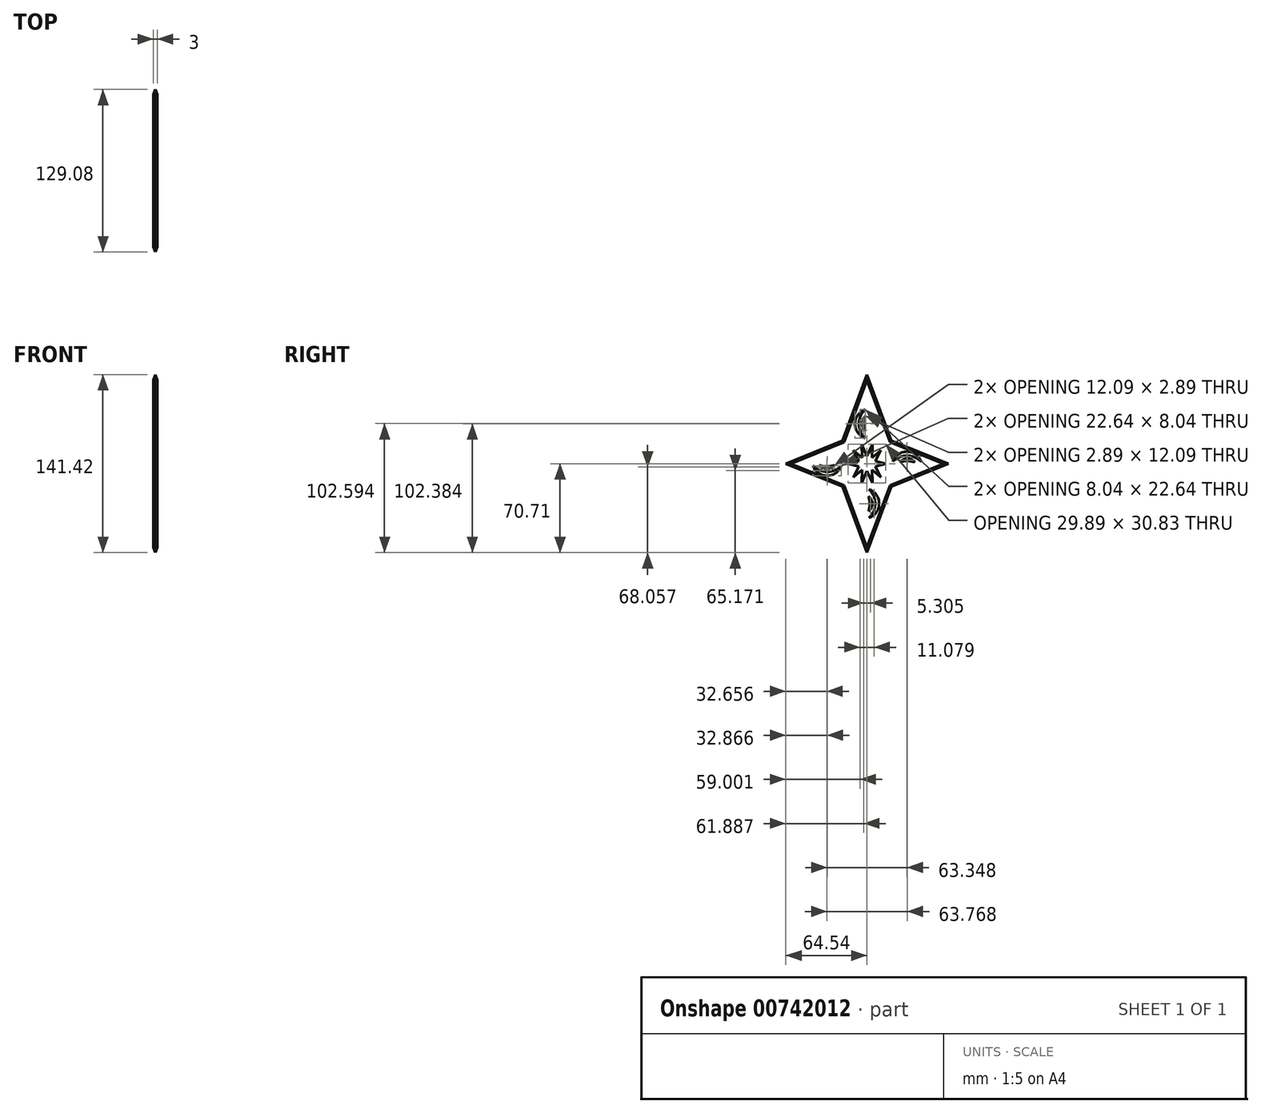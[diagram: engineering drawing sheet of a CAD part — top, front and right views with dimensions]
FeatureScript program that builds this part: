
annotation { "Feature Type Name" : "Feature", "Feature Type Description" : "" }
export const myFeature = defineFeature(function(context is Context, id is Id, definition is map)
    precondition{}
    {
        {
            var Q0;
            Q0=qCreatedBy(makeId("Right.planeOp"),FACE);
            var sketch = newSketch(context, id + "F0", { "sketchPlane" : qUnion([Q0])});
            skLineSegment(sketch, "E0", {"start": v(0, -70.7) * mm, "end": v(-19.36, -18.32) * mm});
            skLineSegment(sketch, "E1", {"start": v(-19.36, -18.32) * mm, "end": v(-64.54, 0) * mm});
            skLineSegment(sketch, "E2.MirrorCS", {"start": v(0, -70.7) * mm, "end": v(19.36, -18.32) * mm});
            skLineSegment(sketch, "E3.MirrorCS", {"start": v(19.36, -18.32) * mm, "end": v(64.54, 0) * mm});
            skLineSegment(sketch, "E4.MirrorCS", {"start": v(-19.36, 18.32) * mm, "end": v(-64.54, 0) * mm});
            skLineSegment(sketch, "E5.MirrorCS", {"start": v(0, 70.7) * mm, "end": v(-19.36, 18.32) * mm});
            skLineSegment(sketch, "E6.MirrorCS", {"start": v(0, 70.7) * mm, "end": v(19.36, 18.32) * mm});
            skLineSegment(sketch, "E7.MirrorCS", {"start": v(19.36, 18.32) * mm, "end": v(64.54, 0) * mm});
            skSolve(sketch);
        }
        {
            var Q0;
            Q0=qSketchRegion(id+"F0",true);
            extrude(context, id + "F1", {"entities" : qUnion([Q0]), "depth" : 3 * mm});
        }
        {
            var Q0;
            Q0=makeQuery(id+"F1.opExtrude","CAP_EDGE",EDGE,{"disambiguationData":[OSD([sQuery(id+"F0.wireOp",EDGE,"E4.MirrorCS")])],"isStart":false});
            var Q1;
            Q1=makeQuery(id+"F1.opExtrude","CAP_EDGE",EDGE,{"disambiguationData":[OSD([sQuery(id+"F0.wireOp",EDGE,"E5.MirrorCS")])],"isStart":false});
            var Q2;
            Q2=makeQuery(id+"F1.opExtrude","CAP_EDGE",EDGE,{"disambiguationData":[OSD([sQuery(id+"F0.wireOp",EDGE,"E5.MirrorCS")])],"isStart":true});
            var Q3;
            Q3=makeQuery(id+"F1.opExtrude","CAP_EDGE",EDGE,{"disambiguationData":[OSD([sQuery(id+"F0.wireOp",EDGE,"E4.MirrorCS")])],"isStart":true});
            var Q4;
            Q4=makeQuery(id+"F1.opExtrude","CAP_EDGE",EDGE,{"disambiguationData":[OSD([sQuery(id+"F0.wireOp",EDGE,"E1")])],"isStart":true});
            var Q5;
            Q5=makeQuery(id+"F1.opExtrude","CAP_EDGE",EDGE,{"disambiguationData":[OSD([sQuery(id+"F0.wireOp",EDGE,"E1")])],"isStart":false});
            var Q6;
            Q6=makeQuery(id+"F1.opExtrude","CAP_EDGE",EDGE,{"disambiguationData":[OSD([sQuery(id+"F0.wireOp",EDGE,"E0")])],"isStart":true});
            var Q7;
            Q7=makeQuery(id+"F1.opExtrude","CAP_EDGE",EDGE,{"disambiguationData":[OSD([sQuery(id+"F0.wireOp",EDGE,"E0")])],"isStart":false});
            var Q8;
            Q8=makeQuery(id+"F1.opExtrude","CAP_EDGE",EDGE,{"disambiguationData":[OSD([sQuery(id+"F0.wireOp",EDGE,"E2.MirrorCS")])],"isStart":false});
            var Q9;
            Q9=makeQuery(id+"F1.opExtrude","CAP_EDGE",EDGE,{"disambiguationData":[OSD([sQuery(id+"F0.wireOp",EDGE,"E2.MirrorCS")])],"isStart":true});
            var Q10;
            Q10=makeQuery(id+"F1.opExtrude","CAP_EDGE",EDGE,{"disambiguationData":[OSD([sQuery(id+"F0.wireOp",EDGE,"E3.MirrorCS")])],"isStart":false});
            var Q11;
            Q11=makeQuery(id+"F1.opExtrude","CAP_EDGE",EDGE,{"disambiguationData":[OSD([sQuery(id+"F0.wireOp",EDGE,"E3.MirrorCS")])],"isStart":true});
            var Q12;
            Q12=makeQuery(id+"F1.opExtrude","CAP_EDGE",EDGE,{"disambiguationData":[OSD([sQuery(id+"F0.wireOp",EDGE,"E6.MirrorCS")])],"isStart":true});
            var Q13;
            Q13=makeQuery(id+"F1.opExtrude","CAP_EDGE",EDGE,{"disambiguationData":[OSD([sQuery(id+"F0.wireOp",EDGE,"E6.MirrorCS")])],"isStart":false});
            var Q14;
            Q14=makeQuery(id+"F1.opExtrude","CAP_EDGE",EDGE,{"disambiguationData":[OSD([sQuery(id+"F0.wireOp",EDGE,"E7.MirrorCS")])],"isStart":false});
            var Q15;
            Q15=makeQuery(id+"F1.opExtrude","CAP_EDGE",EDGE,{"disambiguationData":[OSD([sQuery(id+"F0.wireOp",EDGE,"E7.MirrorCS")])],"isStart":true});
            chamfer(context, id + "F2", {"entities" : qUnion([Q0, Q1, Q2, Q3, Q4, Q5, Q6, Q7, Q8, Q9, Q10, Q11, Q12, Q13, Q14, Q15]), "width" : 1.5 * mm, "tangentPropagation" : true});
        }
        {
            var Q0;
            Q0=qCreatedBy(makeId("Right.planeOp"),FACE);
            var sketch = newSketch(context, id + "F3", { "sketchPlane" : qUnion([Q0])});
            skLineSegment(sketch, "E8", {"start": v(0, -5.89) * mm, "end": v(4.3, -15.41) * mm});
            skLineSegment(sketch, "E9", {"start": v(4.3, -15.41) * mm, "end": v(4.11, -4.76) * mm});
            skLineSegment(sketch, "E10.MirrorCS", {"start": v(0, -5.89) * mm, "end": v(-4.3, -15.41) * mm});
            skLineSegment(sketch, "E11.MirrorCS", {"start": v(-4.3, -15.41) * mm, "end": v(-4.11, -4.76) * mm});
            skLineSegment(sketch, "E12.MirrorCS", {"start": v(-4.3, 15.41) * mm, "end": v(-4.11, 4.76) * mm});
            skLineSegment(sketch, "E13.MirrorCS", {"start": v(0, 5.89) * mm, "end": v(-4.3, 15.41) * mm});
            skLineSegment(sketch, "E14.MirrorCS", {"start": v(0, 5.89) * mm, "end": v(4.3, 15.41) * mm});
            skLineSegment(sketch, "E15.MirrorCS", {"start": v(4.3, 15.41) * mm, "end": v(4.11, 4.76) * mm});
            skLineSegment(sketch, "E16", {"start": v(-4.11, -4.76) * mm, "end": v(-10.84, -10.74) * mm});
            skLineSegment(sketch, "E17", {"start": v(-10.84, -10.74) * mm, "end": v(-6.54, -2.15) * mm});
            skLineSegment(sketch, "E18", {"start": v(-6.54, -2.15) * mm, "end": v(-14.95, 0) * mm});
            skLineSegment(sketch, "E19.MirrorCS", {"start": v(-6.54, 2.15) * mm, "end": v(-14.95, 0) * mm});
            skLineSegment(sketch, "E20.MirrorCS", {"start": v(-10.84, 10.74) * mm, "end": v(-6.54, 2.15) * mm});
            skLineSegment(sketch, "E21.MirrorCS", {"start": v(-4.11, 4.76) * mm, "end": v(-10.84, 10.74) * mm});
            skLineSegment(sketch, "E22.MirrorCS", {"start": v(6.54, 2.15) * mm, "end": v(14.95, 0) * mm});
            skLineSegment(sketch, "E23.MirrorCS", {"start": v(10.84, 10.74) * mm, "end": v(6.54, 2.15) * mm});
            skLineSegment(sketch, "E24.MirrorCS", {"start": v(4.11, 4.76) * mm, "end": v(10.84, 10.74) * mm});
            skLineSegment(sketch, "E25.MirrorCS", {"start": v(10.84, -10.74) * mm, "end": v(6.54, -2.15) * mm});
            skLineSegment(sketch, "E26.MirrorCS", {"start": v(4.11, -4.76) * mm, "end": v(10.84, -10.74) * mm});
            skLineSegment(sketch, "E27.MirrorCS", {"start": v(6.54, -2.15) * mm, "end": v(14.95, 0) * mm});
            skSolve(sketch);
        }
        {
            var Q0;
            Q0=qSketchRegion(id+"F3",true);
            extrude(context, id + "F4", {"entities" : qUnion([Q0]), "operationType" : NewBodyOperationType.REMOVE, "depth" : 25 * mm});
        }
        {
            var Q0;
            Q0=qCreatedBy(makeId("Right.planeOp"),FACE);
            var sketch = newSketch(context, id + "F5", { "sketchPlane" : qUnion([Q0])});
            skArc(sketch, "E28", {"start": v(1.2, -37.93) * mm, "mid": v(4.1, -31.88) * mm, "end": v(1.2, -25.84) * mm});
            skArc(sketch, "E29", {"start": v(1.2, -37.93) * mm, "mid": v(2.13, -31.88) * mm, "end": v(1.2, -25.84) * mm});
            skArc(sketch, "E30", {"start": v(1.52, -43) * mm, "mid": v(9.56, -31.67) * mm, "end": v(1.52, -20.35) * mm});
            skArc(sketch, "E31", {"start": v(1.52, -43) * mm, "mid": v(6.41, -31.67) * mm, "end": v(1.52, -20.35) * mm});
            skArc(sketch, "E32.MirrorCS", {"start": v(-1.2, -37.93) * mm, "mid": v(-4.1, -31.88) * mm, "end": v(-1.2, -25.84) * mm});
            skArc(sketch, "E33.MirrorCS", {"start": v(-1.2, -37.93) * mm, "mid": v(-2.13, -31.88) * mm, "end": v(-1.2, -25.84) * mm});
            skArc(sketch, "E34.MirrorCS", {"start": v(-1.52, -43) * mm, "mid": v(-6.41, -31.67) * mm, "end": v(-1.52, -20.35) * mm});
            skArc(sketch, "E35.MirrorCS", {"start": v(-1.52, -43) * mm, "mid": v(-9.56, -31.67) * mm, "end": v(-1.52, -20.35) * mm});
            skSolve(sketch);
        }
        {
            var Q0;
            Q0=makeQuery(id+"F5.imprint","IMPRINT",FACE,{"disambiguationData":[TD([[makeQuery(id+"F5.imprint","IMPRINT",EDGE,{"derivedFrom":sQuery(id+"F5.wireOp",EDGE,"E34.MirrorCS")}),1.0]])]});
            var Q1;
            Q1=makeQuery(id+"F5.imprint","IMPRINT",FACE,{"disambiguationData":[TD([[makeQuery(id+"F5.imprint","IMPRINT",EDGE,{"derivedFrom":sQuery(id+"F5.wireOp",EDGE,"E32.MirrorCS")}),-1.0]])]});
            var Q2;
            Q2=makeQuery(id+"F5.imprint","IMPRINT",FACE,{"disambiguationData":[TD([[makeQuery(id+"F5.imprint","IMPRINT",EDGE,{"derivedFrom":sQuery(id+"F5.wireOp",EDGE,"E30")}),1.0]])]});
            var Q3;
            Q3=makeQuery(id+"F5.imprint","IMPRINT",FACE,{"disambiguationData":[TD([[makeQuery(id+"F5.imprint","IMPRINT",EDGE,{"derivedFrom":sQuery(id+"F5.wireOp",EDGE,"E28")}),1.0]])]});
            extrude(context, id + "F6", {"entities" : qUnion([Q0, Q1, Q2, Q3]), "operationType" : NewBodyOperationType.REMOVE, "endBound" : BoundingType.THROUGH_ALL, "depth" : 2 * mm});
        }
        {
            var Q0;
            Q0=qCreatedBy(makeId("Front.planeOp"),FACE);
            var sketch = newSketch(context, id + "F7", { "sketchPlane" : qUnion([Q0])});
            skLineSegment(sketch, "E36", {"start": v(0, 0) * mm, "end": v(-49.38, 0) * mm});
            skSolve(sketch);
        }
        {
            var Q0;
            Q0=makeQuery(id+"F1.opExtrude","SWEPT_BODY",BODY,{"disambiguationData":[OSD([sQuery(id+"F0.wireOp",EDGE,"E0"),sQuery(id+"F0.wireOp",EDGE,"E1"),sQuery(id+"F0.wireOp",EDGE,"E2.MirrorCS"),sQuery(id+"F0.wireOp",EDGE,"E3.MirrorCS"),sQuery(id+"F0.wireOp",EDGE,"E4.MirrorCS"),sQuery(id+"F0.wireOp",EDGE,"E5.MirrorCS"),sQuery(id+"F0.wireOp",EDGE,"E6.MirrorCS"),sQuery(id+"F0.wireOp",EDGE,"E7.MirrorCS")])]});
            var Q1;
            Q1=makeQuery(id+"F6.boolean.opBoolean","COPY",FACE,{"derivedFrom":makeQuery(id+"F6.opExtrude","SWEPT_FACE",FACE,{"disambiguationData":[OSD([sQuery(id+"F5.wireOp",EDGE,"E35.MirrorCS")])]})});
            var Q2;
            Q2=makeQuery(id+"F6.boolean.opBoolean","COPY",FACE,{"derivedFrom":makeQuery(id+"F6.opExtrude","SWEPT_FACE",FACE,{"disambiguationData":[OSD([sQuery(id+"F5.wireOp",EDGE,"E32.MirrorCS")])]})});
            var Q3;
            Q3=makeQuery(id+"F6.boolean.opBoolean","COPY",FACE,{"derivedFrom":makeQuery(id+"F6.opExtrude","SWEPT_FACE",FACE,{"disambiguationData":[OSD([sQuery(id+"F5.wireOp",EDGE,"E29")])]})});
            var Q4;
            Q4=makeQuery(id+"F6.boolean.opBoolean","COPY",FACE,{"derivedFrom":makeQuery(id+"F6.opExtrude","SWEPT_FACE",FACE,{"disambiguationData":[OSD([sQuery(id+"F5.wireOp",EDGE,"E31")])]})});
            var Q5;
            Q5=makeQuery(id+"F6.boolean.opBoolean","COPY",FACE,{"derivedFrom":makeQuery(id+"F6.opExtrude","SWEPT_FACE",FACE,{"disambiguationData":[OSD([sQuery(id+"F5.wireOp",EDGE,"E34.MirrorCS")])]})});
            var Q6;
            Q6=makeQuery(id+"F6.boolean.opBoolean","COPY",FACE,{"derivedFrom":makeQuery(id+"F6.opExtrude","SWEPT_FACE",FACE,{"disambiguationData":[OSD([sQuery(id+"F5.wireOp",EDGE,"E33.MirrorCS")])]})});
            var Q7;
            Q7=makeQuery(id+"F6.boolean.opBoolean","COPY",FACE,{"derivedFrom":makeQuery(id+"F6.opExtrude","SWEPT_FACE",FACE,{"disambiguationData":[OSD([sQuery(id+"F5.wireOp",EDGE,"E28")])]})});
            var Q8;
            Q8=makeQuery(id+"F6.boolean.opBoolean","COPY",FACE,{"derivedFrom":makeQuery(id+"F6.opExtrude","SWEPT_FACE",FACE,{"disambiguationData":[OSD([sQuery(id+"F5.wireOp",EDGE,"E30")])]})});
            var Q9;
            Q9=sQuery(id+"F7.wireOp",EDGE,"E36");
            circularPattern(context, id + "F8", {"operationType" : NewBodyOperationType.REMOVE, "faces" : qUnion([Q1, Q2, Q3, Q4, Q5, Q6, Q7, Q8]), "axis" : qUnion([Q9]), "angle" : 360 * degree, "instanceCount" : 4, "equalSpace" : true, "patternType" : PatternType.FACE});
        }
    });
